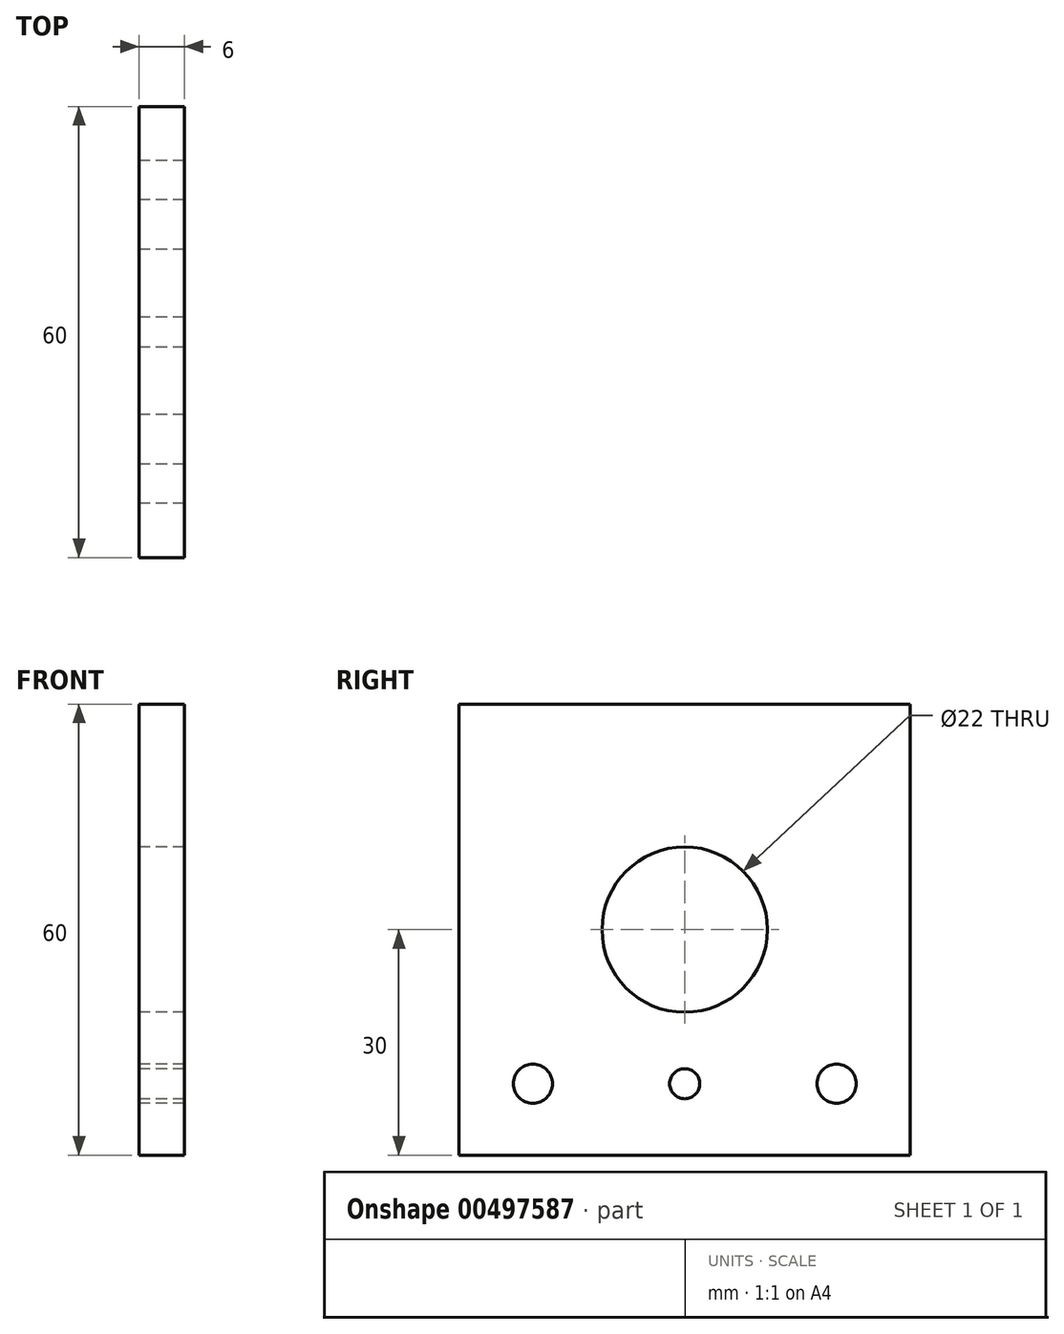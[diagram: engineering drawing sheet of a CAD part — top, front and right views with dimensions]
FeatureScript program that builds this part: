
annotation { "Feature Type Name" : "Feature", "Feature Type Description" : "" }
export const myFeature = defineFeature(function(context is Context, id is Id, definition is map)
    precondition{}
    {
        {
            var Q0;
            Q0=qCreatedBy(makeId("Right.planeOp"),FACE);
            var sketch = newSketch(context, id + "F0", { "sketchPlane" : qUnion([Q0])});
            skLineSegment(sketch, "E0.bottom", {"start": v(0, 0) * mm, "end": v(60, 0) * mm});
            skLineSegment(sketch, "E0.top", {"start": v(0, 60) * mm, "end": v(60, 60) * mm});
            skLineSegment(sketch, "E0.left", {"start": v(0, 0) * mm, "end": v(0, 60) * mm});
            skLineSegment(sketch, "E0.right", {"start": v(60, 0) * mm, "end": v(60, 60) * mm});
            skLineSegment(sketch, "E1", {"start": v(30, 60) * mm, "end": v(30, 0) * mm, "construction": true});
            skCircle(sketch, "E2", {"center": v(30, 30) * mm, "radius": 11 * mm});
            skCircle(sketch, "E3", {"center": v(30, 30) * mm, "radius": 9.5 * mm, "construction": true});
            skCircle(sketch, "E4", {"center": v(30, 9.5) * mm, "radius": 2 * mm});
            skCircle(sketch, "E5", {"center": v(9.8, 9.5) * mm, "radius": 2.6 * mm});
            skCircle(sketch, "E6.MirrorC", {"center": v(50.2, 9.5) * mm, "radius": 2.6 * mm});
            skSolve(sketch);
        }
        {
            var Q0;
            Q0 = qSketchRegion(id + "F0", true);
            extrude(context, id + "F1", {"entities" : qUnion([Q0]), "depth" : 6 * mm, "offsetDistance" : 25.4 * mm});
        }
    });
